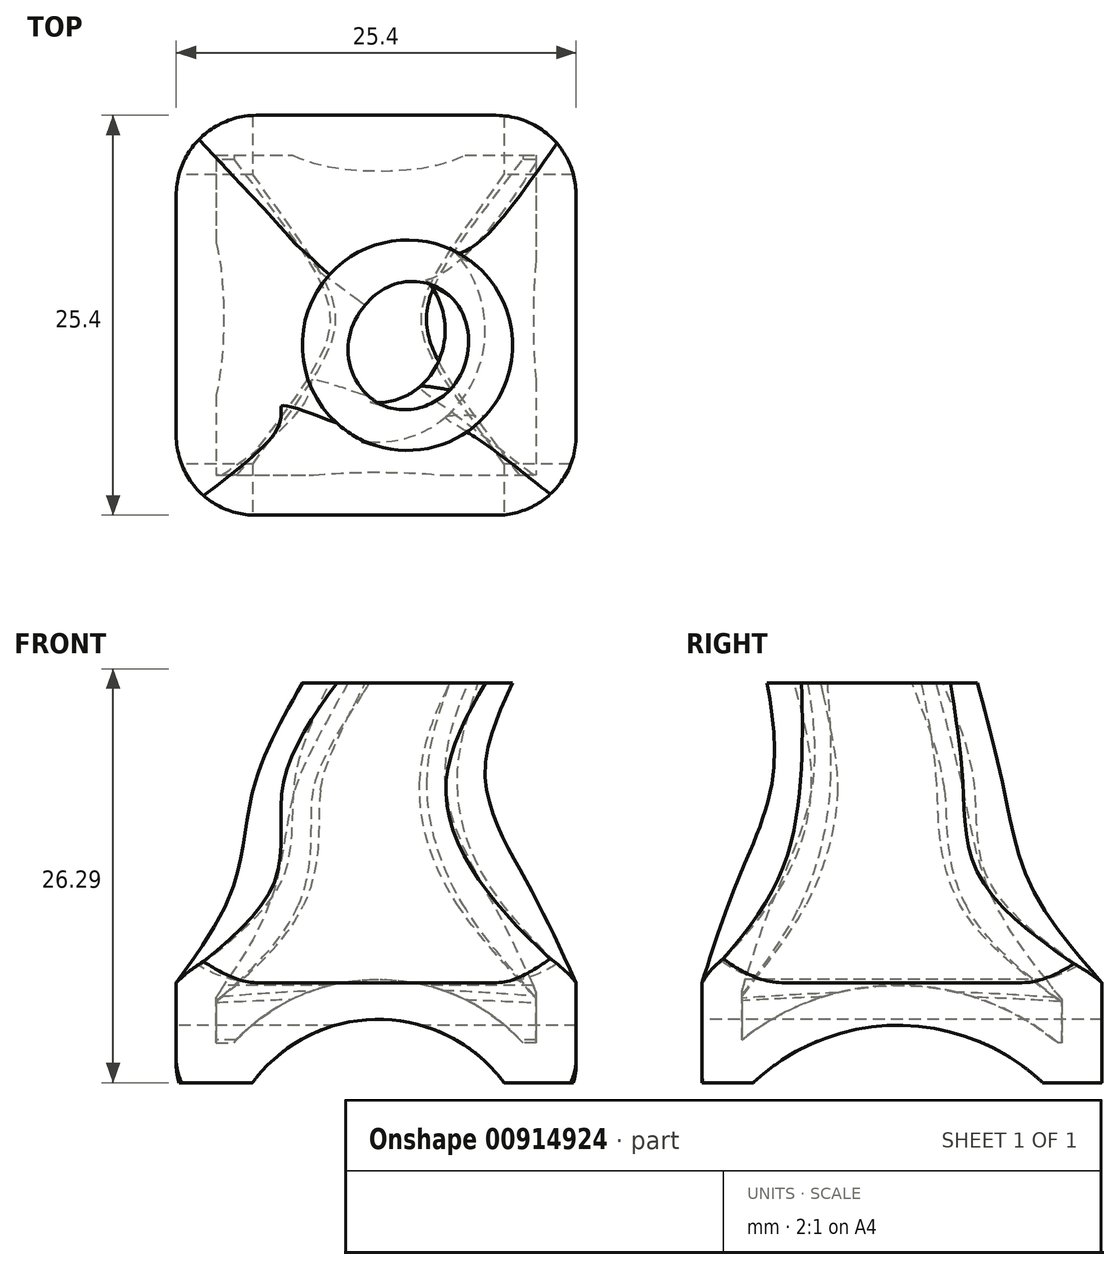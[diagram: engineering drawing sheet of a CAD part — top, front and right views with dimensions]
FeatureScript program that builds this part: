
annotation { "Feature Type Name" : "Feature", "Feature Type Description" : "" }
export const myFeature = defineFeature(function(context is Context, id is Id, definition is map)
    precondition{}
    {
        {
            var Q0;
            Q0=qCreatedBy(makeId("Top.planeOp"),FACE);
            var sketch = newSketch(context, id + "F0", { "sketchPlane" : qUnion([Q0])});
            skLineSegment(sketch, "E0.bottom", {"start": v(-12.7, 12.7) * mm, "end": v(12.7, 12.7) * mm});
            skLineSegment(sketch, "E0.top", {"start": v(-12.7, -12.7) * mm, "end": v(12.7, -12.7) * mm});
            skLineSegment(sketch, "E0.left", {"start": v(-12.7, 12.7) * mm, "end": v(-12.7, -12.7) * mm});
            skLineSegment(sketch, "E0.right", {"start": v(12.7, 12.7) * mm, "end": v(12.7, -12.7) * mm});
            skPoint(sketch, "E0.middle", {"position": v(0, 0) * mm});
            skSolve(sketch);
        }
        {
            var Q0;
            Q0=makeQuery(id+"F0.imprint","IMPRINT",FACE,{"disambiguationData":[TD([[makeQuery(id+"F0.imprint","IMPRINT",EDGE,{"derivedFrom":sQuery(id+"F0.wireOp",EDGE,"E0.bottom")}),-1.0]])]});
            extrude(context, id + "F1", {"entities" : qUnion([Q0]), "depth" : 6.35 * mm, "offsetDistance" : 25.4 * mm});
        }
        {
            var Q0;
            Q0=makeQuery(id+"F1.opExtrude","CAP_FACE",FACE,{"disambiguationData":[OSD([sQuery(id+"F0.wireOp",EDGE,"E0.bottom"),sQuery(id+"F0.wireOp",EDGE,"E0.top"),sQuery(id+"F0.wireOp",EDGE,"E0.left"),sQuery(id+"F0.wireOp",EDGE,"E0.right")])],"isStart":false});
            var sketch = newSketch(context, id + "F2", { "sketchPlane" : qUnion([Q0])});
            skLineSegment(sketch, "E1.bottom", {"start": v(-3.56, 3.67) * mm, "end": v(3.56, 3.67) * mm});
            skLineSegment(sketch, "E1.top", {"start": v(-3.56, -3.67) * mm, "end": v(3.56, -3.67) * mm});
            skLineSegment(sketch, "E1.left", {"start": v(-3.56, 3.67) * mm, "end": v(-3.56, -3.67) * mm});
            skLineSegment(sketch, "E1.right", {"start": v(3.56, 3.67) * mm, "end": v(3.56, -3.67) * mm});
            skPoint(sketch, "E1.middle", {"position": v(0, 0) * mm});
            skSolve(sketch);
        }
        {
            var Q0;
            Q0=makeQuery(id+"F1.opExtrude","SWEPT_FACE",FACE,{"disambiguationData":[OSD([sQuery(id+"F0.wireOp",EDGE,"E0.bottom")])]});
            var sketch = newSketch(context, id + "F3", { "sketchPlane" : qUnion([Q0])});
            skLineSegment(sketch, "E2.bottom", {"start": v(-12.7, 0) * mm, "end": v(12.7, 0) * mm});
            skLineSegment(sketch, "E2.top", {"start": v(-12.7, 25.4) * mm, "end": v(12.7, 25.4) * mm});
            skLineSegment(sketch, "E2.left", {"start": v(-12.7, 0) * mm, "end": v(-12.7, 25.4) * mm});
            skLineSegment(sketch, "E2.right", {"start": v(12.7, 0) * mm, "end": v(12.7, 25.4) * mm});
            skSolve(sketch);
        }
        {
            var Q0;
            Q0=makeQuery(id+"F1.opExtrude","SWEPT_FACE",FACE,{"disambiguationData":[OSD([sQuery(id+"F0.wireOp",EDGE,"E0.top")])]});
            var sketch = newSketch(context, id + "F4", { "sketchPlane" : qUnion([Q0])});
            skArc(sketch, "E3", {"start": v(8.12, 0) * mm, "mid": v(0.14, 4.02) * mm, "end": v(-7.85, 0) * mm});
            skLineSegment(sketch, "E4", {"start": v(-7.85, 0) * mm, "end": v(8.12, 0) * mm});
            skSolve(sketch);
        }
        {
            var Q0;
            Q0=makeQuery(id+"F1.opExtrude","SWEPT_FACE",FACE,{"disambiguationData":[OSD([sQuery(id+"F0.wireOp",EDGE,"E0.left")])]});
            var sketch = newSketch(context, id + "F5", { "sketchPlane" : qUnion([Q0])});
            skArc(sketch, "E5", {"start": v(9.44, 0) * mm, "mid": v(0.25, 3.64) * mm, "end": v(-8.93, 0) * mm});
            skLineSegment(sketch, "E6", {"start": v(-8.93, 0) * mm, "end": v(9.44, 0) * mm});
            skSolve(sketch);
        }
        {
            var Q0;
            Q0=makeQuery(id+"F1.opExtrude","CAP_FACE",FACE,{"disambiguationData":[OSD([sQuery(id+"F0.wireOp",EDGE,"E0.bottom"),sQuery(id+"F0.wireOp",EDGE,"E0.top"),sQuery(id+"F0.wireOp",EDGE,"E0.left"),sQuery(id+"F0.wireOp",EDGE,"E0.right")])],"isStart":false});
            var sketch = newSketch(context, id + "F6", { "sketchPlane" : qUnion([Q0])});
            skLineSegment(sketch, "E7", {"start": v(10.15, -9.96) * mm, "end": v(-10.67, -9.96) * mm});
            skLineSegment(sketch, "E8", {"start": v(-10.67, -9.96) * mm, "end": v(-10.67, 8.23) * mm});
            skLineSegment(sketch, "E9", {"start": v(-10.67, 8.23) * mm, "end": v(-10.67, 10.85) * mm});
            skLineSegment(sketch, "E10", {"start": v(-10.67, 10.85) * mm, "end": v(11.17, 10.85) * mm});
            skLineSegment(sketch, "E11", {"start": v(11.17, 10.85) * mm, "end": v(11.17, -9.96) * mm});
            skSolve(sketch);
        }
        {
            var Q0;
            Q0=makeQuery(id+"F5.imprint","IMPRINT",FACE,{"disambiguationData":[TD([[makeQuery(id+"F5.imprint","IMPRINT",EDGE,{"derivedFrom":sQuery(id+"F5.wireOp",EDGE,"E5")}),1.0]])]});
            extrude(context, id + "F7", {"entities" : qUnion([Q0]), "operationType" : NewBodyOperationType.REMOVE, "oppositeDirection" : true, "depth" : 60.7 * mm, "offsetDistance" : 25.4 * mm});
        }
        {
            var Q0;
            Q0=makeQuery(id+"F4.imprint","IMPRINT",FACE,{"disambiguationData":[TD([[makeQuery(id+"F4.imprint","IMPRINT",EDGE,{"derivedFrom":sQuery(id+"F4.wireOp",EDGE,"E3")}),1.0]])]});
            extrude(context, id + "F8", {"entities" : qUnion([Q0]), "operationType" : NewBodyOperationType.REMOVE, "oppositeDirection" : true, "depth" : 80.26 * mm, "offsetDistance" : 25.4 * mm});
        }
        {
            var Q0;
            Q0=makeQuery(id+"F2.imprint","IMPRINT",FACE,{"disambiguationData":[TD([[makeQuery(id+"F2.imprint","IMPRINT",EDGE,{"derivedFrom":sQuery(id+"F2.wireOp",EDGE,"E1.bottom")}),1.0]])]});
            cPlane(context, id + "F9", {"entities" : qUnion([Q0]), "cplaneType" : CPlaneType.OFFSET, "offset" : 6.35 * mm, "width" : 152.4 * mm, "height" : 152.4 * mm});
        }
        {
            var Q0;
            Q0=qCreatedBy(id+"F9.planeOp",FACE);
            cPlane(context, id + "F10", {"entities" : qUnion([Q0]), "cplaneType" : CPlaneType.OFFSET, "offset" : 6.35 * mm, "width" : 152.4 * mm, "height" : 152.4 * mm});
        }
        {
            var Q0;
            Q0=qCreatedBy(id+"F9.planeOp",FACE);
            var sketch = newSketch(context, id + "F11", { "sketchPlane" : qUnion([Q0])});
            skCircle(sketch, "E12", {"center": v(0.3, -1.2) * mm, "radius": 9.3 * mm});
            skSolve(sketch);
        }
        {
            var Q0;
            Q0=qCreatedBy(id+"F10.planeOp",FACE);
            cPlane(context, id + "F12", {"entities" : qUnion([Q0]), "cplaneType" : CPlaneType.OFFSET, "offset" : 6.35 * mm, "width" : 152.4 * mm, "height" : 152.4 * mm});
        }
        {
            var Q0;
            Q0=qCreatedBy(id+"F10.planeOp",FACE);
            var sketch = newSketch(context, id + "F13", { "sketchPlane" : qUnion([Q0])});
            skCircle(sketch, "E13", {"center": v(-0.37, -0.93) * mm, "radius": 7.32 * mm});
            skSolve(sketch);
        }
        {
            var Q0;
            Q0=qCreatedBy(id+"F12.planeOp",FACE);
            var sketch = newSketch(context, id + "F14", { "sketchPlane" : qUnion([Q0])});
            skCircle(sketch, "E14", {"center": v(1.99, -1.9) * mm, "radius": 6.68 * mm});
            skSolve(sketch);
        }
        {
            var Q1;
            Q1=makeQuery(id+"F6.imprint","IMPRINT",FACE,{"disambiguationData":[TD([[makeQuery(id+"F6.imprint","IMPRINT",EDGE,{"derivedFrom":makeQuery(id+"F1.opExtrude","CAP_EDGE",EDGE,{"disambiguationData":[OSD([sQuery(id+"F0.wireOp",EDGE,"E0.bottom")])],"isStart":false})}),-1.0]])]});
            var Q2;
            Q2=makeQuery(id+"F11.imprint","IMPRINT",FACE,{"disambiguationData":[TD([[makeQuery(id+"F11.imprint","IMPRINT",EDGE,{"derivedFrom":sQuery(id+"F11.wireOp",EDGE,"E12")}),1.0]])]});
            var Q3;
            Q3=makeQuery(id+"F13.imprint","IMPRINT",FACE,{"disambiguationData":[TD([[makeQuery(id+"F13.imprint","IMPRINT",EDGE,{"derivedFrom":sQuery(id+"F13.wireOp",EDGE,"E13")}),1.0]])]});
            var Q4;
            Q4=makeQuery(id+"F14.imprint","IMPRINT",FACE,{"disambiguationData":[TD([[makeQuery(id+"F14.imprint","IMPRINT",EDGE,{"derivedFrom":sQuery(id+"F14.wireOp",EDGE,"E14")}),1.0]])]});
            loft(context, id + "F15", {"operationType" : NewBodyOperationType.ADD, "sheetProfilesArray" : [{ "sheetProfileEntities" : qUnion([Q1]) }, { "sheetProfileEntities" : qUnion([Q2]) }, { "sheetProfileEntities" : qUnion([Q3]) }, { "sheetProfileEntities" : qUnion([Q4]) }]});
        }
        {
            var Q0;
            Q0=makeQuery(id+"F15.opLoft","CAP_FACE",FACE,{"disambiguationData":[OSD([makeQuery(id+"F14.imprint","IMPRINT",FACE,{"disambiguationData":[TD([[makeQuery(id+"F14.imprint","IMPRINT",EDGE,{"derivedFrom":sQuery(id+"F14.wireOp",EDGE,"E14")}),1.0]])]})])],"isStart":true});
            shell(context, id + "F16", {"entities" : qUnion([Q0]), "thickness" : 2.54 * mm});
        }
        {
            var Q0;
            Q0=makeQuery(id+"F1.opExtrude","SWEPT_EDGE",EDGE,{"disambiguationData":[OSD([sQuery(id+"F0.wireOp",EDGE,"E0.bottom"),sQuery(id+"F0.wireOp",EDGE,"E0.left")])]});
            var Q1;
            Q1=makeQuery(id+"F1.opExtrude","SWEPT_EDGE",EDGE,{"disambiguationData":[OSD([sQuery(id+"F0.wireOp",EDGE,"E0.top"),sQuery(id+"F0.wireOp",EDGE,"E0.left")])]});
            var Q2;
            Q2=makeQuery(id+"F1.opExtrude","SWEPT_EDGE",EDGE,{"disambiguationData":[OSD([sQuery(id+"F0.wireOp",EDGE,"E0.top"),sQuery(id+"F0.wireOp",EDGE,"E0.right")])]});
            var Q3;
            Q3=makeQuery(id+"F1.opExtrude","SWEPT_EDGE",EDGE,{"disambiguationData":[OSD([sQuery(id+"F0.wireOp",EDGE,"E0.bottom"),sQuery(id+"F0.wireOp",EDGE,"E0.right")])]});
            fillet(context, id + "F17", {"entities" : qUnion([Q0, Q1, Q2, Q3]), "radius" : 5.08 * mm, "tangentPropagation" : true, "allowEdgeOverflow" : false});
        }
    });
